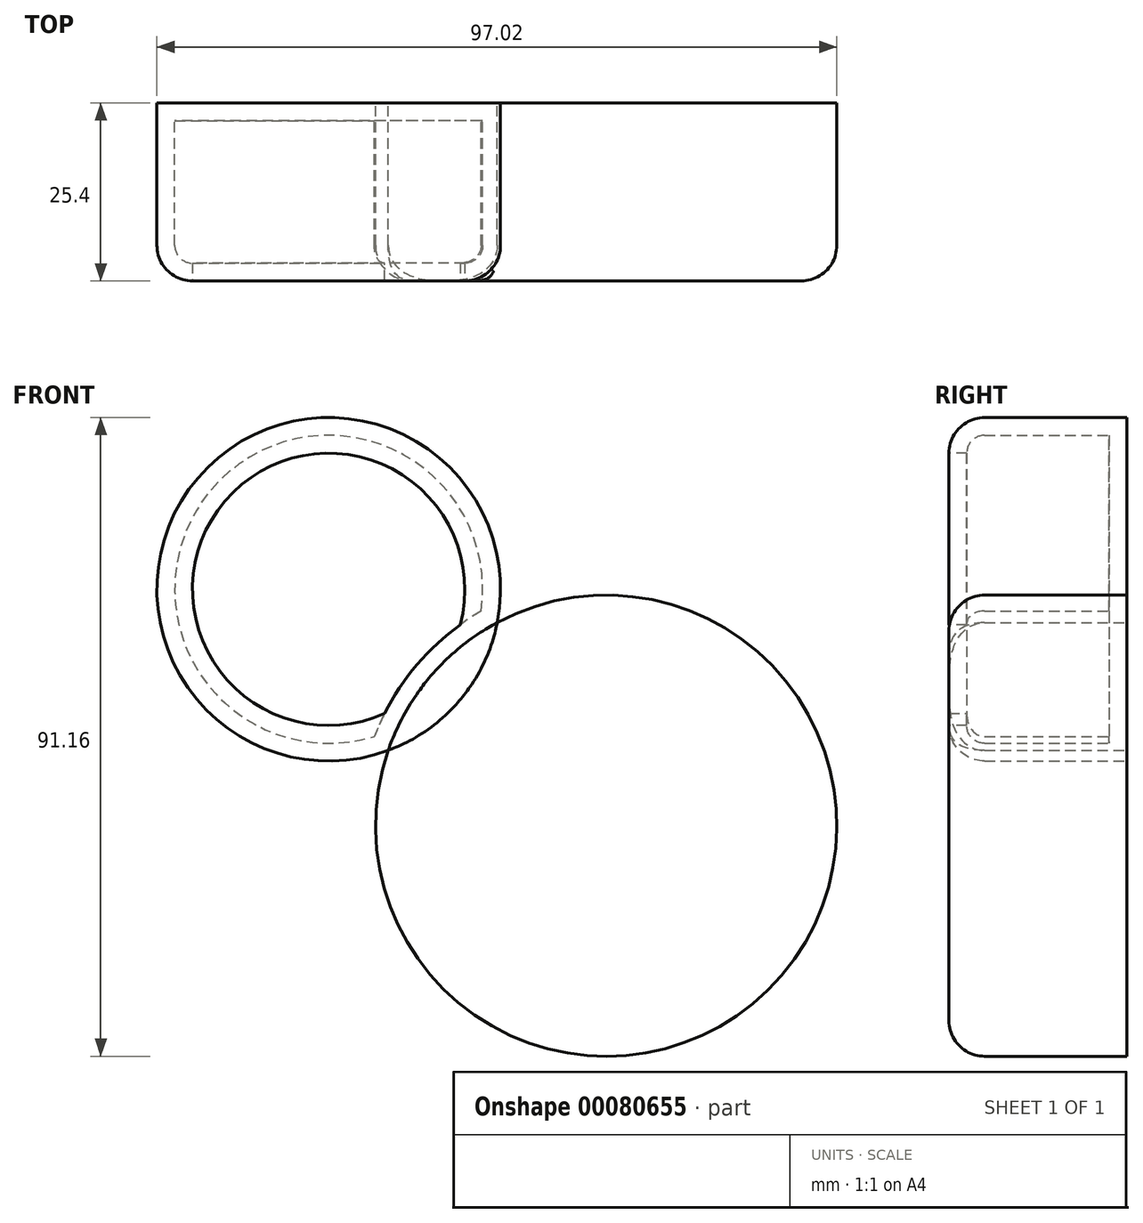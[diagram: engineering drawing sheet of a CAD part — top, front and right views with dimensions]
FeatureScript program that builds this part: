
annotation { "Feature Type Name" : "Feature", "Feature Type Description" : "" }
export const myFeature = defineFeature(function(context is Context, id is Id, definition is map)
    precondition{}
    {
        {
            var Q0;
            Q0=qCreatedBy(makeId("Front.planeOp"),FACE);
            var sketch = newSketch(context, id + "F0", { "sketchPlane" : qUnion([Q0])});
            skCircle(sketch, "E0", {"center": v(-48.97, 39.24) * mm, "radius": 24.51 * mm});
            skCircle(sketch, "E1", {"center": v(-9.37, 5.5) * mm, "radius": 32.9 * mm});
            skSolve(sketch);
        }
        {
            var Q0;
            {var subQ0=sQuery(id+"F0.wireOp",EDGE,"E1");var subQ1=sQuery(id+"F0.wireOp",EDGE,"E0");var subQ2=makeQuery(id+"F0.imprint","INTERSECT",VERTEX,{"disambiguationData":[OD(0.0)],"derivedFrom":[subQ1,subQ0]});Q0=makeQuery(id+"F0.imprint","IMPRINT",FACE,{"disambiguationData":[TD([[makeQuery(id+"F0.imprint","IMPRINT",EDGE,{"disambiguationData":[TD([[subQ2,1.0]])],"derivedFrom":subQ1}),1.0]])]});}
            var sketch = newSketch(context, id + "F1", { "sketchPlane" : qUnion([Q0])});
            skSolve(sketch);
        }
        {
            var Q0;
            Q0 = qSketchRegion(id + "F1", true);
            var Q1;
            {var subQ0=sQuery(id+"F0.wireOp",EDGE,"E1");var subQ1=sQuery(id+"F0.wireOp",EDGE,"E0");var subQ2=makeQuery(id+"F0.imprint","INTERSECT",VERTEX,{"disambiguationData":[OD(0.0)],"derivedFrom":[subQ1,subQ0]});Q1=makeQuery(id+"F0.imprint","IMPRINT",FACE,{"disambiguationData":[TD([[makeQuery(id+"F0.imprint","IMPRINT",EDGE,{"disambiguationData":[TD([[subQ2,1.0]])],"derivedFrom":subQ1}),1.0]])]});}
            var Q2;
            {var subQ0=sQuery(id+"F0.wireOp",EDGE,"E1");var subQ1=sQuery(id+"F0.wireOp",EDGE,"E0");var subQ2=makeQuery(id+"F0.imprint","INTERSECT",VERTEX,{"disambiguationData":[OD(0.0)],"derivedFrom":[subQ1,subQ0]});Q2=makeQuery(id+"F0.imprint","IMPRINT",FACE,{"disambiguationData":[TD([[makeQuery(id+"F0.imprint","IMPRINT",EDGE,{"disambiguationData":[TD([[subQ2,-1.0]])],"derivedFrom":subQ1}),-1.0]])]});}
            extrude(context, id + "F2", {"entities" : qUnion([Q0, Q1, Q2]), "depth" : 25.4 * mm});
        }
        {
            var Q0;
            {var subQ0=sQuery(id+"F0.wireOp",EDGE,"E1");var subQ1=sQuery(id+"F0.wireOp",EDGE,"E0");Q0=makeQuery(id+"F2.opExtrude","CAP_EDGE",EDGE,{"disambiguationData":[OSD([subQ1]),TDD([makeQuery(id+"F0.imprint","IMPRINT",EDGE,{"disambiguationData":[TD([[makeQuery(id+"F0.imprint","INTERSECT",VERTEX,{"disambiguationData":[OD(0.0)],"derivedFrom":[subQ1,subQ0]}),1.0]])],"derivedFrom":subQ1})])],"isStart":false});}
            var Q1;
            {var subQ0=sQuery(id+"F0.wireOp",EDGE,"E1");var subQ1=sQuery(id+"F0.wireOp",EDGE,"E0");Q1=makeQuery(id+"F2.opExtrude","CAP_EDGE",EDGE,{"disambiguationData":[OSD([subQ0]),TDD([makeQuery(id+"F0.imprint","IMPRINT",EDGE,{"disambiguationData":[TD([[makeQuery(id+"F0.imprint","INTERSECT",VERTEX,{"disambiguationData":[OD(0.0)],"derivedFrom":[subQ1,subQ0]}),-1.0]])],"derivedFrom":subQ0})])],"isStart":false});}
            fillet(context, id + "F3", {"entities" : qUnion([Q0, Q1]), "radius" : 5.08 * mm, "tangentPropagation" : true, "allowEdgeOverflow" : false});
        }
        {
            var Q0;
            {var subQ0=sQuery(id+"F0.wireOp",EDGE,"E1");var subQ1=sQuery(id+"F0.wireOp",EDGE,"E0");var subQ2=makeQuery(id+"F0.imprint","INTERSECT",VERTEX,{"disambiguationData":[OD(0.0)],"derivedFrom":[subQ1,subQ0]});Q0=makeQuery(id+"F2.opExtrude","CAP_FACE",FACE,{"disambiguationData":[OSD([subQ1,subQ0]),TDD([makeQuery(id+"F0.imprint","IMPRINT",EDGE,{"disambiguationData":[TD([[subQ2,1.0]])],"derivedFrom":subQ1}),makeQuery(id+"F0.imprint","IMPRINT",EDGE,{"disambiguationData":[TD([[subQ2,1.0]])],"derivedFrom":subQ0})])],"isStart":false});}
            shell(context, id + "F4", {"entities" : qUnion([Q0]), "thickness" : 2.54 * mm});
        }
    });
